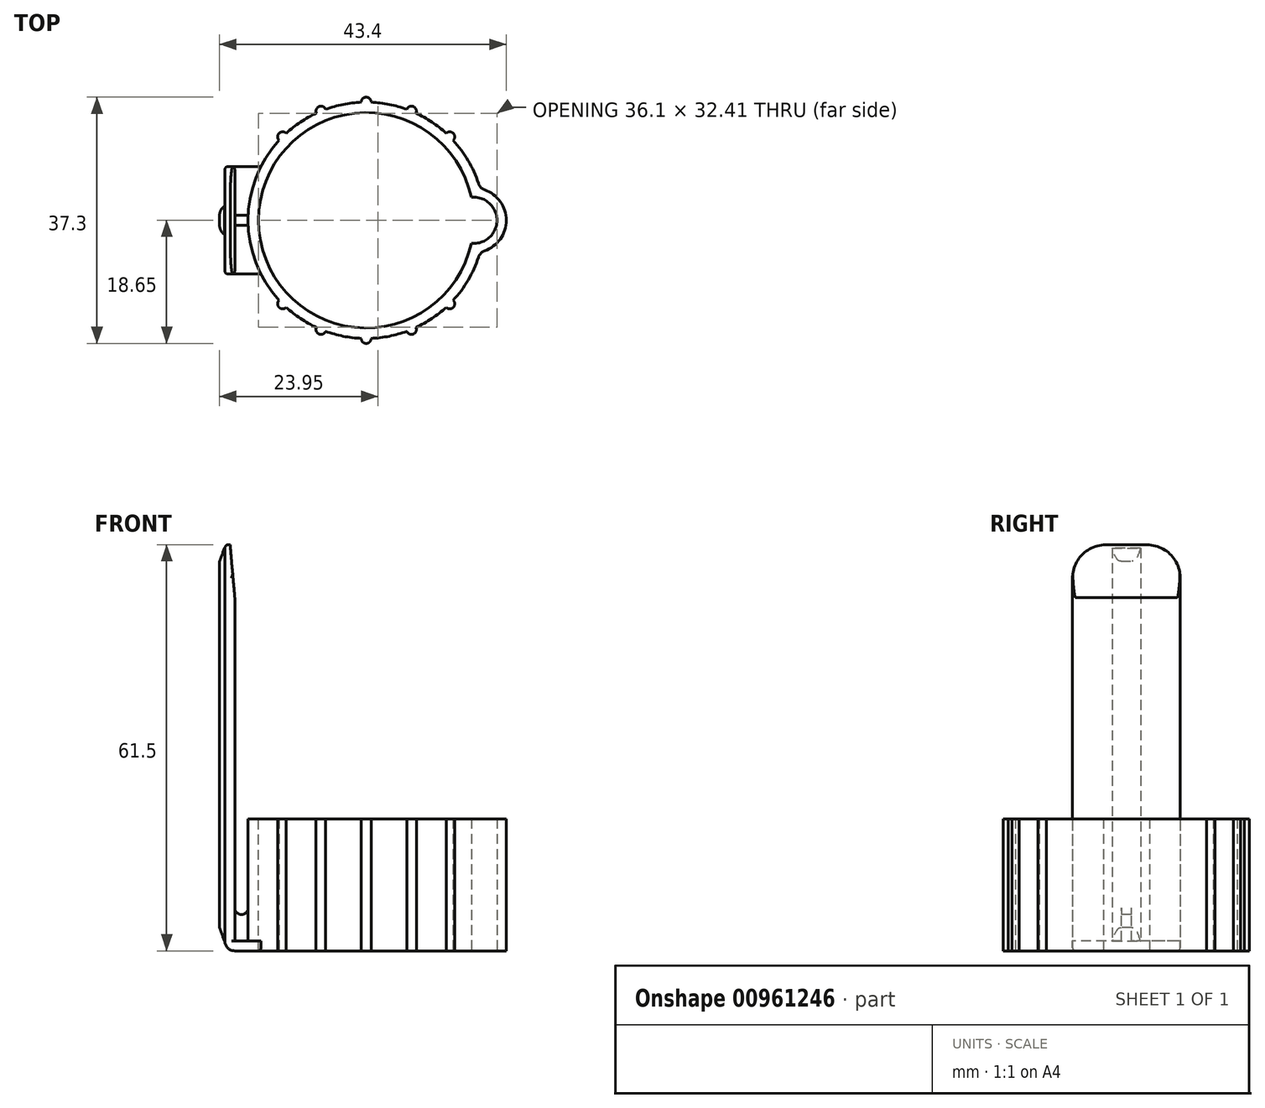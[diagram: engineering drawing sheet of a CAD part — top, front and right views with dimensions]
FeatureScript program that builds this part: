
annotation { "Feature Type Name" : "Feature", "Feature Type Description" : "" }
export const myFeature = defineFeature(function(context is Context, id is Id, definition is map)
    precondition{}
    {
        {
            var Q0;
            Q0=qCreatedBy(makeId("Top.planeOp"),FACE);
            var sketch = newSketch(context, id + "F0", { "sketchPlane" : qUnion([Q0])});
            skCircle(sketch, "E0", {"center": v(0, 0) * mm, "radius": 17.9 * mm});
            skCircle(sketch, "E1", {"center": v(0, 0) * mm, "radius": 16.3 * mm});
            skSolve(sketch);
        }
        {
            var Q0;
            Q0=makeQuery(id+"F0.imprint","IMPRINT",FACE,{"disambiguationData":[TD([[makeQuery(id+"F0.imprint","IMPRINT",EDGE,{"derivedFrom":sQuery(id+"F0.wireOp",EDGE,"E0")}),1.0]])]});
            extrude(context, id + "F1", {"entities" : qUnion([Q0]), "oppositeDirection" : true, "depth" : 20 * mm, "offsetDistance" : 25 * mm});
        }
        {
            var Q0;
            Q0=makeQuery(id+"F1.opExtrude","CAP_FACE",FACE,{"disambiguationData":[OSD([sQuery(id+"F0.wireOp",EDGE,"E0"),sQuery(id+"F0.wireOp",EDGE,"sRQzcW8V-2rlP-Dt0l-GWwx-olrQuQmdxicd")])],"isStart":false});
            var sketch = newSketch(context, id + "F2", { "sketchPlane" : qUnion([Q0])});
            skCircle(sketch, "E2.0", {"center": v(0, 0) * mm, "radius": 17.9 * mm});
            skCircle(sketch, "E3", {"center": v(0, 17.9) * mm, "radius": 0.75 * mm});
            skCircle(sketch, "E4.1.0", {"center": v(-6.85, 16.54) * mm, "radius": 0.75 * mm});
            skCircle(sketch, "E4.2.0", {"center": v(-12.66, 12.66) * mm, "radius": 0.75 * mm});
            skCircle(sketch, "E4.6.0", {"center": v(-12.66, -12.66) * mm, "radius": 0.75 * mm});
            skCircle(sketch, "E4.7.0", {"center": v(-6.85, -16.54) * mm, "radius": 0.75 * mm});
            skCircle(sketch, "E5.1.8.0", {"center": v(0, -17.9) * mm, "radius": 0.75 * mm});
            skCircle(sketch, "E5.1.9.0", {"center": v(6.85, -16.54) * mm, "radius": 0.75 * mm});
            skCircle(sketch, "E5.1.10.0", {"center": v(12.66, -12.66) * mm, "radius": 0.75 * mm});
            skCircle(sketch, "E5.1.11.0", {"center": v(16.54, -6.85) * mm, "radius": 0.75 * mm});
            skCircle(sketch, "E5.1.13.0", {"center": v(16.54, 6.85) * mm, "radius": 0.75 * mm});
            skCircle(sketch, "E5.1.14.0", {"center": v(12.66, 12.66) * mm, "radius": 0.75 * mm});
            skCircle(sketch, "E5.1.15.0", {"center": v(6.85, 16.54) * mm, "radius": 0.75 * mm});
            skLineSegment(sketch, "E6", {"start": v(0, 0) * mm, "end": v(19.2, 0) * mm});
            skLineSegment(sketch, "E7", {"start": v(0, 0) * mm, "end": v(-19.9, 0) * mm});
            skCircle(sketch, "E8.1.0", {"center": v(-16.54, 6.85) * mm, "radius": 0.75 * mm});
            skCircle(sketch, "E8.2.0", {"center": v(-17.9, 0) * mm, "radius": 0.75 * mm});
            skCircle(sketch, "E8.3.0", {"center": v(-16.54, -6.85) * mm, "radius": 0.75 * mm});
            skLineSegment(sketch, "E8.anchor1", {"start": v(0, 0) * mm, "end": v(-12.66, 12.66) * mm, "construction": true});
            skLineSegment(sketch, "E8.anchor2", {"start": v(0, 0) * mm, "end": v(-12.66, -12.66) * mm, "construction": true});
            skLineSegment(sketch, "E9", {"start": v(-21.4, 8.15) * mm, "end": v(-21.4, -8.15) * mm});
            skCircle(sketch, "E10", {"center": v(16.3, 0) * mm, "radius": 3.5 * mm});
            skCircle(sketch, "E11.0", {"center": v(16.3, 0) * mm, "radius": 4.9 * mm});
            skLineSegment(sketch, "E12", {"start": v(-21.4, 8.15) * mm, "end": v(-15.94, 8.15) * mm});
            skLineSegment(sketch, "E13.MirrorCS", {"start": v(-21.4, -8.15) * mm, "end": v(-15.94, -8.15) * mm});
            skSolve(sketch);
        }
        {
            var Q0;
            {var subQ0=sQuery(id+"F2.wireOp",EDGE,"E5.1.10.0");var subQ1=sQuery(id+"F2.wireOp",EDGE,"E2.0");var subQ2=makeQuery(id+"F2.imprint","INTERSECT",VERTEX,{"disambiguationData":[OD(0.0)],"derivedFrom":[subQ1,subQ0]});Q0=makeQuery(id+"F2.imprint","IMPRINT",FACE,{"disambiguationData":[TD([[makeQuery(id+"F2.imprint","IMPRINT",EDGE,{"disambiguationData":[TD([[subQ2,-1.0]])],"derivedFrom":subQ1}),1.0]])]});}
            var Q1;
            {var subQ0=sQuery(id+"F2.wireOp",EDGE,"E5.1.9.0");var subQ1=sQuery(id+"F2.wireOp",EDGE,"E2.0");var subQ2=makeQuery(id+"F2.imprint","INTERSECT",VERTEX,{"disambiguationData":[OD(0.0)],"derivedFrom":[subQ1,subQ0]});Q1=makeQuery(id+"F2.imprint","IMPRINT",FACE,{"disambiguationData":[TD([[makeQuery(id+"F2.imprint","IMPRINT",EDGE,{"disambiguationData":[TD([[subQ2,-1.0]])],"derivedFrom":subQ1}),1.0]])]});}
            var Q2;
            {var subQ0=sQuery(id+"F2.wireOp",EDGE,"E5.1.8.0");var subQ1=sQuery(id+"F2.wireOp",EDGE,"E2.0");var subQ2=makeQuery(id+"F2.imprint","INTERSECT",VERTEX,{"disambiguationData":[OD(0.0)],"derivedFrom":[subQ1,subQ0]});Q2=makeQuery(id+"F2.imprint","IMPRINT",FACE,{"disambiguationData":[TD([[makeQuery(id+"F2.imprint","IMPRINT",EDGE,{"disambiguationData":[TD([[subQ2,-1.0]])],"derivedFrom":subQ1}),1.0]])]});}
            var Q3;
            {var subQ0=sQuery(id+"F2.wireOp",EDGE,"E4.7.0");var subQ1=sQuery(id+"F2.wireOp",EDGE,"E2.0");var subQ2=makeQuery(id+"F2.imprint","INTERSECT",VERTEX,{"disambiguationData":[OD(0.0)],"derivedFrom":[subQ1,subQ0]});Q3=makeQuery(id+"F2.imprint","IMPRINT",FACE,{"disambiguationData":[TD([[makeQuery(id+"F2.imprint","IMPRINT",EDGE,{"disambiguationData":[TD([[subQ2,-1.0]])],"derivedFrom":subQ1}),1.0]])]});}
            var Q4;
            {var subQ0=sQuery(id+"F2.wireOp",EDGE,"E4.6.0");var subQ1=sQuery(id+"F2.wireOp",EDGE,"E2.0");var subQ2=makeQuery(id+"F2.imprint","INTERSECT",VERTEX,{"disambiguationData":[OD(0.0)],"derivedFrom":[subQ1,subQ0]});Q4=makeQuery(id+"F2.imprint","IMPRINT",FACE,{"disambiguationData":[TD([[makeQuery(id+"F2.imprint","IMPRINT",EDGE,{"disambiguationData":[TD([[subQ2,-1.0]])],"derivedFrom":subQ1}),1.0]])]});}
            var Q5;
            {var subQ0=sQuery(id+"F2.wireOp",EDGE,"E4.5.0");var subQ1=sQuery(id+"F2.wireOp",EDGE,"E2.0");var subQ2=makeQuery(id+"F2.imprint","INTERSECT",VERTEX,{"disambiguationData":[OD(0.0)],"derivedFrom":[subQ1,subQ0]});Q5=makeQuery(id+"F2.imprint","IMPRINT",FACE,{"disambiguationData":[TD([[makeQuery(id+"F2.imprint","IMPRINT",EDGE,{"disambiguationData":[TD([[subQ2,-1.0]])],"derivedFrom":subQ1}),1.0]])]});}
            var Q6;
            {var subQ0=sQuery(id+"F2.wireOp",EDGE,"E4.4.0");var subQ1=sQuery(id+"F2.wireOp",EDGE,"E2.0");var subQ2=makeQuery(id+"F2.imprint","INTERSECT",VERTEX,{"disambiguationData":[OD(0.0)],"derivedFrom":[subQ1,subQ0]});Q6=makeQuery(id+"F2.imprint","IMPRINT",FACE,{"disambiguationData":[TD([[makeQuery(id+"F2.imprint","IMPRINT",EDGE,{"disambiguationData":[TD([[subQ2,-1.0]])],"derivedFrom":subQ1}),1.0]])]});}
            var Q7;
            {var subQ0=sQuery(id+"F2.wireOp",EDGE,"E4.3.0");var subQ1=sQuery(id+"F2.wireOp",EDGE,"E2.0");var subQ2=makeQuery(id+"F2.imprint","INTERSECT",VERTEX,{"disambiguationData":[OD(0.0)],"derivedFrom":[subQ1,subQ0]});Q7=makeQuery(id+"F2.imprint","IMPRINT",FACE,{"disambiguationData":[TD([[makeQuery(id+"F2.imprint","IMPRINT",EDGE,{"disambiguationData":[TD([[subQ2,-1.0]])],"derivedFrom":subQ1}),1.0]])]});}
            var Q8;
            {var subQ0=sQuery(id+"F2.wireOp",EDGE,"E4.2.0");var subQ1=sQuery(id+"F2.wireOp",EDGE,"E2.0");var subQ2=makeQuery(id+"F2.imprint","INTERSECT",VERTEX,{"disambiguationData":[OD(0.0)],"derivedFrom":[subQ1,subQ0]});Q8=makeQuery(id+"F2.imprint","IMPRINT",FACE,{"disambiguationData":[TD([[makeQuery(id+"F2.imprint","IMPRINT",EDGE,{"disambiguationData":[TD([[subQ2,-1.0]])],"derivedFrom":subQ1}),1.0]])]});}
            var Q9;
            {var subQ0=sQuery(id+"F2.wireOp",EDGE,"E4.1.0");var subQ1=sQuery(id+"F2.wireOp",EDGE,"E2.0");var subQ2=makeQuery(id+"F2.imprint","INTERSECT",VERTEX,{"disambiguationData":[OD(0.0)],"derivedFrom":[subQ1,subQ0]});Q9=makeQuery(id+"F2.imprint","IMPRINT",FACE,{"disambiguationData":[TD([[makeQuery(id+"F2.imprint","IMPRINT",EDGE,{"disambiguationData":[TD([[subQ2,-1.0]])],"derivedFrom":subQ1}),1.0]])]});}
            var Q10;
            {var subQ0=sQuery(id+"F2.wireOp",EDGE,"E3");var subQ1=sQuery(id+"F2.wireOp",EDGE,"E2.0");var subQ2=makeQuery(id+"F2.imprint","INTERSECT",VERTEX,{"disambiguationData":[OD(0.0)],"derivedFrom":[subQ1,subQ0]});Q10=makeQuery(id+"F2.imprint","IMPRINT",FACE,{"disambiguationData":[TD([[makeQuery(id+"F2.imprint","IMPRINT",EDGE,{"disambiguationData":[TD([[subQ2,-1.0]])],"derivedFrom":subQ1}),1.0]])]});}
            var Q11;
            {var subQ0=sQuery(id+"F2.wireOp",EDGE,"E5.1.15.0");var subQ1=sQuery(id+"F2.wireOp",EDGE,"E2.0");var subQ2=makeQuery(id+"F2.imprint","INTERSECT",VERTEX,{"disambiguationData":[OD(0.0)],"derivedFrom":[subQ1,subQ0]});Q11=makeQuery(id+"F2.imprint","IMPRINT",FACE,{"disambiguationData":[TD([[makeQuery(id+"F2.imprint","IMPRINT",EDGE,{"disambiguationData":[TD([[subQ2,-1.0]])],"derivedFrom":subQ1}),1.0]])]});}
            var Q12;
            {var subQ0=sQuery(id+"F2.wireOp",EDGE,"E5.1.14.0");var subQ1=sQuery(id+"F2.wireOp",EDGE,"E2.0");var subQ2=makeQuery(id+"F2.imprint","INTERSECT",VERTEX,{"disambiguationData":[OD(0.0)],"derivedFrom":[subQ1,subQ0]});Q12=makeQuery(id+"F2.imprint","IMPRINT",FACE,{"disambiguationData":[TD([[makeQuery(id+"F2.imprint","IMPRINT",EDGE,{"disambiguationData":[TD([[subQ2,-1.0]])],"derivedFrom":subQ1}),1.0]])]});}
            var Q13;
            {var subQ0=sQuery(id+"F2.wireOp",EDGE,"E5.1.12.0");var subQ1=sQuery(id+"F2.wireOp",EDGE,"E2.0");var subQ2=makeQuery(id+"F2.imprint","INTERSECT",VERTEX,{"disambiguationData":[OD(0.0)],"derivedFrom":[subQ1,subQ0]});Q13=makeQuery(id+"F2.imprint","IMPRINT",FACE,{"disambiguationData":[TD([[makeQuery(id+"F2.imprint","IMPRINT",EDGE,{"disambiguationData":[TD([[subQ2,1.0]])],"derivedFrom":subQ1}),1.0]])]});}
            var Q14;
            {var subQ0=sQuery(id+"F2.wireOp",EDGE,"386c1725-cd85-426e-880f-386daac7d9d5.0");var subQ1=sQuery(id+"F2.wireOp",EDGE,"E2.0");var subQ2=makeQuery(id+"F2.imprint","INTERSECT",VERTEX,{"disambiguationData":[OD(0.0)],"derivedFrom":[subQ1,subQ0]});Q14=makeQuery(id+"F2.imprint","IMPRINT",FACE,{"disambiguationData":[TD([[makeQuery(id+"F2.imprint","IMPRINT",EDGE,{"disambiguationData":[TD([[subQ2,1.0]])],"derivedFrom":subQ1}),1.0]])]});}
            var Q15;
            {var subQ0=sQuery(id+"F2.wireOp",EDGE,"E4.6.0");var subQ1=sQuery(id+"F2.wireOp",EDGE,"E2.0");var subQ2=makeQuery(id+"F2.imprint","INTERSECT",VERTEX,{"disambiguationData":[OD(0.0)],"derivedFrom":[subQ1,subQ0]});Q15=makeQuery(id+"F2.imprint","IMPRINT",FACE,{"disambiguationData":[TD([[makeQuery(id+"F2.imprint","IMPRINT",EDGE,{"disambiguationData":[TD([[subQ2,-1.0]])],"derivedFrom":subQ1}),1.0]])]});}
            var Q16;
            {var subQ0=sQuery(id+"F2.wireOp",EDGE,"E11.0");var subQ1=sQuery(id+"F2.wireOp",EDGE,"E2.0");var subQ2=makeQuery(id+"F2.imprint","INTERSECT",VERTEX,{"disambiguationData":[OD(0.0)],"derivedFrom":[subQ1,subQ0]});Q16=makeQuery(id+"F2.imprint","IMPRINT",FACE,{"disambiguationData":[TD([[makeQuery(id+"F2.imprint","IMPRINT",EDGE,{"disambiguationData":[TD([[subQ2,1.0]])],"derivedFrom":subQ1}),1.0]])]});}
            var Q17;
            Q17=makeQuery(id+"F1.opExtrude","CAP_FACE",FACE,{"disambiguationData":[OSD([sQuery(id+"F0.wireOp",EDGE,"E0"),sQuery(id+"F0.wireOp",EDGE,"E1")])],"isStart":true});
            extrude(context, id + "F3", {"entities" : qUnion([Q0, Q1, Q2, Q3, Q4, Q5, Q6, Q7, Q8, Q9, Q10, Q11, Q12, Q13, Q14, Q15, Q16]), "operationType" : NewBodyOperationType.ADD, "endBound" : BoundingType.UP_TO_SURFACE, "oppositeDirection" : true, "depth" : 25 * mm, "endBoundEntityFace" : qUnion([Q17]), "offsetDistance" : 25 * mm});
        }
        {
            var Q0;
            {var subQ0=sQuery(id+"F2.wireOp",EDGE,"E2.0");Q0=makeQuery(id+"F3.boolean.opBoolean","MERGE",FACE,{"derivedFrom":[makeQuery(id+"FnFO8i2DjUKFFR7_0.opExtrude","CAP_FACE",FACE,{"disambiguationData":[OSD([sQuery(id+"F0.wireOp",EDGE,"E0"),sQuery(id+"F0.wireOp",EDGE,"E1")])],"isStart":false}),makeQuery(id+"F3.opExtrude","CAP_FACE",FACE,{"disambiguationData":[OSD([subQ0,sQuery(id+"F2.wireOp",EDGE,"E5.1.11.0")])],"isStart":false}),makeQuery(id+"F3.opExtrude","CAP_FACE",FACE,{"disambiguationData":[OSD([subQ0,sQuery(id+"F2.wireOp",EDGE,"E5.1.10.0")])],"isStart":false}),makeQuery(id+"F3.opExtrude","CAP_FACE",FACE,{"disambiguationData":[OSD([subQ0,sQuery(id+"F2.wireOp",EDGE,"E5.1.9.0")])],"isStart":false}),makeQuery(id+"F3.opExtrude","CAP_FACE",FACE,{"disambiguationData":[OSD([subQ0,sQuery(id+"F2.wireOp",EDGE,"E5.1.8.0")])],"isStart":false}),makeQuery(id+"F3.opExtrude","CAP_FACE",FACE,{"disambiguationData":[OSD([subQ0,sQuery(id+"F2.wireOp",EDGE,"E4.7.0")])],"isStart":false}),makeQuery(id+"F3.opExtrude","CAP_FACE",FACE,{"disambiguationData":[OSD([subQ0,sQuery(id+"F2.wireOp",EDGE,"E4.6.0")])],"isStart":false}),makeQuery(id+"F3.opExtrude","CAP_FACE",FACE,{"disambiguationData":[OSD([subQ0,sQuery(id+"F2.wireOp",EDGE,"E4.5.0")])],"isStart":false}),makeQuery(id+"F3.opExtrude","CAP_FACE",FACE,{"disambiguationData":[OSD([subQ0,sQuery(id+"F2.wireOp",EDGE,"E4.4.0")])],"isStart":false}),makeQuery(id+"F3.opExtrude","CAP_FACE",FACE,{"disambiguationData":[OSD([subQ0,sQuery(id+"F2.wireOp",EDGE,"E4.3.0")])],"isStart":false}),makeQuery(id+"F3.opExtrude","CAP_FACE",FACE,{"disambiguationData":[OSD([subQ0,sQuery(id+"F2.wireOp",EDGE,"E4.2.0")])],"isStart":false}),makeQuery(id+"F3.opExtrude","CAP_FACE",FACE,{"disambiguationData":[OSD([subQ0,sQuery(id+"F2.wireOp",EDGE,"E4.1.0")])],"isStart":false}),makeQuery(id+"F3.opExtrude","CAP_FACE",FACE,{"disambiguationData":[OSD([subQ0,sQuery(id+"F2.wireOp",EDGE,"E3")])],"isStart":false}),makeQuery(id+"F3.opExtrude","CAP_FACE",FACE,{"disambiguationData":[OSD([subQ0,sQuery(id+"F2.wireOp",EDGE,"E5.1.15.0")])],"isStart":false}),makeQuery(id+"F3.opExtrude","CAP_FACE",FACE,{"disambiguationData":[OSD([subQ0,sQuery(id+"F2.wireOp",EDGE,"E5.1.14.0")])],"isStart":false}),makeQuery(id+"F3.opExtrude","CAP_FACE",FACE,{"disambiguationData":[OSD([subQ0,sQuery(id+"F2.wireOp",EDGE,"E5.1.13.0")])],"isStart":false}),makeQuery(id+"F3.opExtrude","CAP_FACE",FACE,{"disambiguationData":[OSD([subQ0,sQuery(id+"F2.wireOp",EDGE,"E5.1.12.0")])],"isStart":false})]});}
            var sketch = newSketch(context, id + "F4", { "sketchPlane" : qUnion([Q0])});
            skCircle(sketch, "E14", {"center": v(0, 0) * mm, "radius": 16.8 * mm});
            skArc(sketch, "E15.0", {"start": v(12.11, 13.18) * mm, "mid": v(9.94, 14.88) * mm, "end": v(7.54, 16.23) * mm});
            skSolve(sketch);
        }
        {
            var Q0;
            {var subQ0=sQuery(id+"F2.wireOp",EDGE,"E8.1.0");var subQ1=sQuery(id+"F2.wireOp",EDGE,"E2.0");var subQ2=makeQuery(id+"F2.imprint","INTERSECT",VERTEX,{"disambiguationData":[OD(0.0)],"derivedFrom":[subQ1,subQ0]});Q0=makeQuery(id+"F2.imprint","IMPRINT",FACE,{"disambiguationData":[TD([[makeQuery(id+"F2.imprint","IMPRINT",EDGE,{"disambiguationData":[TD([[subQ2,-1.0]])],"derivedFrom":subQ1}),1.0]])]});}
            var Q1;
            {var subQ0=sQuery(id+"F2.wireOp",EDGE,"E7");var subQ1=sQuery(id+"F2.wireOp",EDGE,"E2.0");var subQ2=makeQuery(id+"F2.imprint","INTERSECT",VERTEX,{"derivedFrom":[subQ1,subQ0]});Q1=makeQuery(id+"F2.imprint","IMPRINT",FACE,{"disambiguationData":[TD([[makeQuery(id+"F2.imprint","IMPRINT",EDGE,{"disambiguationData":[TD([[subQ2,-1.0]])],"derivedFrom":subQ1}),1.0]])]});}
            var Q2;
            {var subQ0=sQuery(id+"F2.wireOp",EDGE,"E8.2.0");var subQ1=sQuery(id+"F2.wireOp",EDGE,"E2.0");var subQ2=makeQuery(id+"F2.imprint","INTERSECT",VERTEX,{"disambiguationData":[OD(0.0)],"derivedFrom":[subQ1,subQ0]});Q2=makeQuery(id+"F2.imprint","IMPRINT",FACE,{"disambiguationData":[TD([[makeQuery(id+"F2.imprint","IMPRINT",EDGE,{"disambiguationData":[TD([[subQ2,-1.0]])],"derivedFrom":subQ1}),1.0]])]});}
            var Q3;
            {var subQ0=sQuery(id+"F2.wireOp",EDGE,"E8.3.0");var subQ1=sQuery(id+"F2.wireOp",EDGE,"E2.0");var subQ2=makeQuery(id+"F2.imprint","INTERSECT",VERTEX,{"disambiguationData":[OD(0.0)],"derivedFrom":[subQ1,subQ0]});Q3=makeQuery(id+"F2.imprint","IMPRINT",FACE,{"disambiguationData":[TD([[makeQuery(id+"F2.imprint","IMPRINT",EDGE,{"disambiguationData":[TD([[subQ2,-1.0]])],"derivedFrom":subQ1}),1.0]])]});}
            var Q4;
            Q4=makeQuery(id+"F2.imprint","IMPRINT",FACE,{"disambiguationData":[TD([[makeQuery(id+"F2.imprint","IMPRINT",EDGE,{"derivedFrom":sQuery(id+"F2.wireOp",EDGE,"E9")}),1.0]])]});
            extrude(context, id + "F5", {"entities" : qUnion([Q0, Q1, Q2, Q3, Q4]), "operationType" : NewBodyOperationType.ADD, "oppositeDirection" : true, "depth" : 1.5 * mm, "offsetDistance" : 25 * mm});
        }
        {
            var Q0;
            {var subQ0=sQuery(id+"F2.wireOp",EDGE,"E6");var subQ1=sQuery(id+"F2.wireOp",EDGE,"E2.0");var subQ2=makeQuery(id+"F2.imprint","INTERSECT",VERTEX,{"derivedFrom":[subQ1,subQ0]});Q0=makeQuery(id+"F2.imprint","IMPRINT",FACE,{"disambiguationData":[TD([[makeQuery(id+"F2.imprint","IMPRINT",EDGE,{"disambiguationData":[TD([[subQ2,1.0]])],"derivedFrom":subQ1}),-1.0]])]});}
            var Q1;
            {var subQ0=sQuery(id+"F2.wireOp",EDGE,"E6");var subQ1=sQuery(id+"F2.wireOp",EDGE,"E2.0");var subQ2=makeQuery(id+"F2.imprint","INTERSECT",VERTEX,{"derivedFrom":[subQ1,subQ0]});Q1=makeQuery(id+"F2.imprint","IMPRINT",FACE,{"disambiguationData":[TD([[makeQuery(id+"F2.imprint","IMPRINT",EDGE,{"disambiguationData":[TD([[subQ2,-1.0]])],"derivedFrom":subQ1}),-1.0]])]});}
            extrude(context, id + "F6", {"entities" : qUnion([Q0, Q1]), "operationType" : NewBodyOperationType.REMOVE, "oppositeDirection" : true, "depth" : 25 * mm, "offsetDistance" : 25 * mm});
        }
        {
            var Q0;
            {var subQ0=sQuery(id+"F2.wireOp",EDGE,"E11.0");var subQ1=sQuery(id+"F2.wireOp",EDGE,"E2.0");Q0=makeQuery(id+"F3.opExtrude","SWEPT_EDGE",EDGE,{"disambiguationData":[OSD([subQ1,subQ0]),TDD([makeQuery(id+"F2.imprint","INTERSECT",VERTEX,{"disambiguationData":[OD(1.0)],"derivedFrom":[subQ1,subQ0]})])]});}
            var Q1;
            {var subQ0=sQuery(id+"F2.wireOp",EDGE,"E11.0");var subQ1=sQuery(id+"F2.wireOp",EDGE,"E2.0");Q1=makeQuery(id+"F3.opExtrude","SWEPT_EDGE",EDGE,{"disambiguationData":[OSD([subQ1,subQ0]),TDD([makeQuery(id+"F2.imprint","INTERSECT",VERTEX,{"disambiguationData":[OD(0.0)],"derivedFrom":[subQ1,subQ0]})])]});}
            var Q2;
            {var subQ0=sQuery(id+"F2.wireOp",EDGE,"E10");var subQ1=sQuery(id+"F0.wireOp",EDGE,"E1");Q2=makeQuery(id+"F6.boolean.opBoolean","COPY",EDGE,{"derivedFrom":makeQuery(id+"F6.opExtrude","SWEPT_EDGE",EDGE,{"disambiguationData":[OSD([subQ1,subQ0]),TDD([makeQuery(id+"F2.imprint","INTERSECT",VERTEX,{"disambiguationData":[OD(1.0)],"derivedFrom":[makeQuery(id+"F1.opExtrude","CAP_EDGE",EDGE,{"disambiguationData":[OSD([subQ1])],"isStart":false}),subQ0]})])]})});}
            var Q3;
            {var subQ0=sQuery(id+"F2.wireOp",EDGE,"E10");var subQ1=sQuery(id+"F0.wireOp",EDGE,"E1");Q3=makeQuery(id+"F6.boolean.opBoolean","COPY",EDGE,{"derivedFrom":makeQuery(id+"F6.opExtrude","SWEPT_EDGE",EDGE,{"disambiguationData":[OSD([subQ1,subQ0]),TDD([makeQuery(id+"F2.imprint","INTERSECT",VERTEX,{"disambiguationData":[OD(0.0)],"derivedFrom":[makeQuery(id+"F1.opExtrude","CAP_EDGE",EDGE,{"disambiguationData":[OSD([subQ1])],"isStart":false}),subQ0]})])]})});}
            fillet(context, id + "F7", {"entities" : qUnion([Q0, Q1, Q2, Q3]), "radius" : 1.5 * mm, "tangentPropagation" : true, "defaultsChanged" : false, "vertexSettings" : [], "allowEdgeOverflow" : false});
        }
        {
            var Q0;
            Q0=qCreatedBy(makeId("Front.planeOp"),FACE);
            var sketch = newSketch(context, id + "F8", { "sketchPlane" : qUnion([Q0])});
            skLineSegment(sketch, "E16.bottom", {"start": v(-41.01, 64.42) * mm, "end": v(41.01, 64.42) * mm});
            skLineSegment(sketch, "E16.top", {"start": v(-41.01, -64.42) * mm, "end": v(41.01, -64.42) * mm});
            skLineSegment(sketch, "E16.left", {"start": v(-41.01, 64.42) * mm, "end": v(-41.01, -64.42) * mm});
            skLineSegment(sketch, "E16.right", {"start": v(41.01, 64.42) * mm, "end": v(41.01, -64.42) * mm});
            skPoint(sketch, "E16.middle", {"position": v(0, 0) * mm});
            skSolve(sketch);
        }
        {
            var Q0;
            Q0=makeQuery(id+"F5.opExtrude","CAP_FACE",FACE,{"disambiguationData":[OSD([sQuery(id+"F2.wireOp",EDGE,"E2.0"),sQuery(id+"F2.wireOp",EDGE,"E9"),sQuery(id+"F2.wireOp",EDGE,"E12"),sQuery(id+"F2.wireOp",EDGE,"E13.MirrorCS")])],"isStart":false});
            var sketch = newSketch(context, id + "F9", { "sketchPlane" : qUnion([Q0])});
            skLineSegment(sketch, "E17.bottom", {"start": v(-21.4, 8.15) * mm, "end": v(-19.9, 8.15) * mm});
            skLineSegment(sketch, "E17.top", {"start": v(-21.4, -8.15) * mm, "end": v(-19.9, -8.15) * mm});
            skLineSegment(sketch, "E17.left", {"start": v(-21.4, 8.15) * mm, "end": v(-21.4, -8.15) * mm});
            skLineSegment(sketch, "E17.right", {"start": v(-19.9, 8.15) * mm, "end": v(-19.9, -8.15) * mm});
            skSolve(sketch);
        }
        {
            var Q0;
            Q0=makeQuery(id+"F9.imprint","IMPRINT",FACE,{"disambiguationData":[TD([[makeQuery(id+"F9.imprint","IMPRINT",EDGE,{"derivedFrom":sQuery(id+"F9.wireOp",EDGE,"E17.bottom")}),-1.0]])]});
            extrude(context, id + "F10", {"entities" : qUnion([Q0]), "operationType" : NewBodyOperationType.ADD, "depth" : 60 * mm, "offsetDistance" : 25 * mm});
        }
        {
            var Q0;
            Q0=makeQuery(id+"F10.opExtrude","CAP_EDGE",EDGE,{"disambiguationData":[OSD([sQuery(id+"F9.wireOp",EDGE,"E17.bottom")])],"isStart":false});
            var Q1;
            Q1=makeQuery(id+"F10.opExtrude","CAP_EDGE",EDGE,{"disambiguationData":[OSD([sQuery(id+"F9.wireOp",EDGE,"E17.top")])],"isStart":false});
            fillet(context, id + "F11", {"entities" : qUnion([Q0, Q1]), "radius" : 5 * mm, "tangentPropagation" : true, "allowEdgeOverflow" : false});
        }
        {
            var Q0;
            Q0=makeQuery(id+"F5.opExtrude","CAP_EDGE",EDGE,{"disambiguationData":[OSD([sQuery(id+"F2.wireOp",EDGE,"E9")])],"isStart":true});
            var Q1;
            Q1=makeQuery(id+"F10.opExtrude","CAP_EDGE",EDGE,{"disambiguationData":[OSD([sQuery(id+"F9.wireOp",EDGE,"E17.right")])],"isStart":true});
            var Q2;
            {var subQ0=sQuery(id+"F2.wireOp",EDGE,"E2.0");var subQ1=sQuery(id+"F2.wireOp",EDGE,"E8.1.0");var subQ3=makeQuery(id+"F2.imprint","INTERSECT",VERTEX,{"disambiguationData":[OD(0.0)],"derivedFrom":[subQ0,subQ1]});var subQ4=sQuery(id+"F2.wireOp",EDGE,"E8.2.0");var subQ5=makeQuery(id+"F2.imprint","INTERSECT",VERTEX,{"disambiguationData":[OD(1.0)],"derivedFrom":[subQ0,subQ4]});var subQ6=makeQuery(id+"F2.imprint","INTERSECT",VERTEX,{"derivedFrom":[subQ0,sQuery(id+"F2.wireOp",EDGE,"E7")]});var subQ7=makeQuery(id+"F2.imprint","INTERSECT",VERTEX,{"disambiguationData":[OD(0.0)],"derivedFrom":[subQ0,subQ4]});var subQ8=sQuery(id+"F2.wireOp",EDGE,"E8.3.0");var subQ9=makeQuery(id+"F2.imprint","INTERSECT",VERTEX,{"disambiguationData":[OD(1.0)],"derivedFrom":[subQ0,subQ8]});var subQ10=makeQuery(id+"F2.imprint","INTERSECT",VERTEX,{"disambiguationData":[OD(0.0)],"derivedFrom":[subQ0,subQ8]});Q2=makeQuery(id+"F5.opExtrude","CAP_EDGE",EDGE,{"disambiguationData":[OSD([subQ0]),TDD([makeQuery(id+"F2.imprint","IMPRINT",EDGE,{"disambiguationData":[TD([[makeQuery(id+"F2.imprint","INTERSECT",VERTEX,{"derivedFrom":[subQ0,sQuery(id+"F2.wireOp",EDGE,"E13.MirrorCS")]}),-1.0]])],"derivedFrom":subQ0}),makeQuery(id+"F2.imprint","IMPRINT",EDGE,{"disambiguationData":[TD([[subQ10,-1.0]])],"derivedFrom":subQ0}),makeQuery(id+"F2.imprint","IMPRINT",EDGE,{"disambiguationData":[TD([[subQ9,-1.0]])],"derivedFrom":subQ0}),makeQuery(id+"F2.imprint","IMPRINT",EDGE,{"disambiguationData":[TD([[subQ7,-1.0]])],"derivedFrom":subQ0}),makeQuery(id+"F2.imprint","IMPRINT",EDGE,{"disambiguationData":[TD([[subQ6,-1.0]])],"derivedFrom":subQ0}),makeQuery(id+"F2.imprint","IMPRINT",EDGE,{"disambiguationData":[TD([[subQ5,-1.0]])],"derivedFrom":subQ0}),makeQuery(id+"F2.imprint","IMPRINT",EDGE,{"disambiguationData":[TD([[subQ3,-1.0]])],"derivedFrom":subQ0}),makeQuery(id+"F2.imprint","IMPRINT",EDGE,{"disambiguationData":[TD([[makeQuery(id+"F2.imprint","INTERSECT",VERTEX,{"derivedFrom":[subQ0,sQuery(id+"F2.wireOp",EDGE,"E12")]}),1.0]])],"derivedFrom":subQ0})])],"isStart":false});}
            var Q3;
            Q3=makeQuery(id+"F5.opExtrude","SWEPT_EDGE",EDGE,{"disambiguationData":[OSD([sQuery(id+"F2.wireOp",EDGE,"E2.0"),sQuery(id+"F2.wireOp",EDGE,"E12")])]});
            var Q4;
            Q4=makeQuery(id+"F5.opExtrude","SWEPT_EDGE",EDGE,{"disambiguationData":[OSD([sQuery(id+"F2.wireOp",EDGE,"E2.0"),sQuery(id+"F2.wireOp",EDGE,"E13.MirrorCS")])]});
            fillet(context, id + "F12", {"entities" : qUnion([Q0, Q1, Q2, Q3, Q4]), "radius" : 1.5 * mm, "tangentPropagation" : true, "allowEdgeOverflow" : false});
        }
        {
            var Q0;
            Q0=makeQuery(id+"F10.opExtrude","CAP_EDGE",EDGE,{"disambiguationData":[OSD([sQuery(id+"F9.wireOp",EDGE,"E17.right")])],"isStart":false});
            chamfer(context, id + "F13", {"entities" : qUnion([Q0]), "chamferType" : ChamferType.OFFSET_ANGLE, "width" : 8 * mm, "oppositeDirection" : false, "angle" : 5 * degree});
        }
        {
            var Q0;
            Q0=makeQuery(id+"F12.opFillet","SPLIT",FACE,{"disambiguationData":[OD(0.0)],"derivedFrom":makeQuery(id+"F5.opExtrude","CAP_FACE",FACE,{"disambiguationData":[OSD([sQuery(id+"F2.wireOp",EDGE,"E2.0"),sQuery(id+"F2.wireOp",EDGE,"E9"),sQuery(id+"F2.wireOp",EDGE,"E12"),sQuery(id+"F2.wireOp",EDGE,"E13.MirrorCS")])],"isStart":false})});
            var sketch = newSketch(context, id + "F14", { "sketchPlane" : qUnion([Q0])});
            skLineSegment(sketch, "E18", {"start": v(0, 0) * mm, "end": v(-24.2, 0) * mm});
            skLineSegment(sketch, "E19.bottom", {"start": v(-20.41, 0) * mm, "end": v(-17.41, 0) * mm});
            skLineSegment(sketch, "E19.top", {"start": v(-20.41, -0.75) * mm, "end": v(-17.41, -0.75) * mm});
            skLineSegment(sketch, "E19.left", {"start": v(-20.41, 0) * mm, "end": v(-20.41, -0.75) * mm});
            skLineSegment(sketch, "E19.right", {"start": v(-17.41, 0) * mm, "end": v(-17.41, -0.75) * mm});
            skLineSegment(sketch, "E20.MirrorCS", {"start": v(-20.41, 0.75) * mm, "end": v(-17.41, 0.75) * mm});
            skLineSegment(sketch, "E21.MirrorCS", {"start": v(-20.41, 0) * mm, "end": v(-20.41, 0.75) * mm});
            skLineSegment(sketch, "E22.MirrorCS", {"start": v(-17.41, 0) * mm, "end": v(-17.41, 0.75) * mm});
            skSolve(sketch);
        }
        {
            var Q0;
            Q0 = qSketchRegion(id + "F14", true);
            extrude(context, id + "F15", {"entities" : qUnion([Q0]), "operationType" : NewBodyOperationType.ADD, "depth" : 4 * mm, "offsetDistance" : 25 * mm});
        }
        {
            var Q0;
            Q0=makeQuery(id+"F15.boolean.opBoolean","INTERSECT",EDGE,{"derivedFrom":[makeQuery(id+"F10.opExtrude","SWEPT_FACE",FACE,{"disambiguationData":[OSD([sQuery(id+"F9.wireOp",EDGE,"E17.right")])]}),makeQuery(id+"F15.opExtrude","CAP_FACE",FACE,{"disambiguationData":[OSD([sQuery(id+"F14.wireOp",EDGE,"E19.top"),sQuery(id+"F14.wireOp",EDGE,"E19.left"),sQuery(id+"F14.wireOp",EDGE,"E19.right"),sQuery(id+"F14.wireOp",EDGE,"E20.MirrorCS"),sQuery(id+"F14.wireOp",EDGE,"E21.MirrorCS"),sQuery(id+"F14.wireOp",EDGE,"E22.MirrorCS")])],"isStart":false})]});
            var Q1;
            {var subQ0=sQuery(id+"F2.wireOp",EDGE,"E5.1.15.0");var subQ1=sQuery(id+"F2.wireOp",EDGE,"E2.0");var subQ2=sQuery(id+"F2.wireOp",EDGE,"E3");var subQ3=sQuery(id+"F2.wireOp",EDGE,"E4.1.0");var subQ4=sQuery(id+"F2.wireOp",EDGE,"E4.2.0");var subQ5=sQuery(id+"F2.wireOp",EDGE,"E4.6.0");var subQ6=sQuery(id+"F2.wireOp",EDGE,"E4.7.0");var subQ7=sQuery(id+"F2.wireOp",EDGE,"E11.0");var subQ8=sQuery(id+"F2.wireOp",EDGE,"E10");var subQ9=sQuery(id+"F0.wireOp",EDGE,"E1");var subQ10=sQuery(id+"F0.wireOp",EDGE,"E0");var subQ11=sQuery(id+"F2.wireOp",EDGE,"E5.1.8.0");var subQ12=sQuery(id+"F2.wireOp",EDGE,"E5.1.10.0");var subQ13=sQuery(id+"F2.wireOp",EDGE,"E5.1.9.0");var subQ14=sQuery(id+"F2.wireOp",EDGE,"E5.1.14.0");Q1=makeQuery(id+"F15.boolean.opBoolean","INTERSECT",EDGE,{"derivedFrom":[makeQuery(id+"F3.boolean.opBoolean","SPLIT",FACE,{"disambiguationData":[TD([makeQuery(id+"F1.opExtrude","CAP_FACE",FACE,{"disambiguationData":[OSD([subQ10,subQ9])],"isStart":true}),makeQuery(id+"F1.opExtrude","CAP_FACE",FACE,{"disambiguationData":[OSD([subQ10,subQ9])],"isStart":false}),makeQuery(id+"F3.opExtrude","CAP_FACE",FACE,{"disambiguationData":[OSD([subQ1,subQ8,subQ7])],"isStart":true}),makeQuery(id+"F3.opExtrude","CAP_FACE",FACE,{"disambiguationData":[OSD([subQ1,subQ8,subQ7])],"isStart":false}),makeQuery(id+"F3.opExtrude","CAP_FACE",FACE,{"disambiguationData":[OSD([subQ1,subQ12])],"isStart":true}),makeQuery(id+"F3.opExtrude","CAP_FACE",FACE,{"disambiguationData":[OSD([subQ1,subQ12])],"isStart":false}),makeQuery(id+"F3.opExtrude","CAP_FACE",FACE,{"disambiguationData":[OSD([subQ1,subQ13])],"isStart":true}),makeQuery(id+"F3.opExtrude","CAP_FACE",FACE,{"disambiguationData":[OSD([subQ1,subQ13])],"isStart":false}),makeQuery(id+"F3.opExtrude","CAP_FACE",FACE,{"disambiguationData":[OSD([subQ1,subQ11])],"isStart":true}),makeQuery(id+"F3.opExtrude","CAP_FACE",FACE,{"disambiguationData":[OSD([subQ1,subQ11])],"isStart":false}),makeQuery(id+"F3.opExtrude","CAP_FACE",FACE,{"disambiguationData":[OSD([subQ1,subQ6])],"isStart":true}),makeQuery(id+"F3.opExtrude","CAP_FACE",FACE,{"disambiguationData":[OSD([subQ1,subQ6])],"isStart":false}),makeQuery(id+"F3.opExtrude","CAP_FACE",FACE,{"disambiguationData":[OSD([subQ1,subQ5])],"isStart":true}),makeQuery(id+"F3.opExtrude","CAP_FACE",FACE,{"disambiguationData":[OSD([subQ1,subQ5])],"isStart":false}),makeQuery(id+"F3.opExtrude","CAP_FACE",FACE,{"disambiguationData":[OSD([subQ1,subQ4])],"isStart":true}),makeQuery(id+"F3.opExtrude","CAP_FACE",FACE,{"disambiguationData":[OSD([subQ1,subQ4])],"isStart":false}),makeQuery(id+"F3.opExtrude","CAP_FACE",FACE,{"disambiguationData":[OSD([subQ1,subQ3])],"isStart":true}),makeQuery(id+"F3.opExtrude","CAP_FACE",FACE,{"disambiguationData":[OSD([subQ1,subQ3])],"isStart":false}),makeQuery(id+"F3.opExtrude","CAP_FACE",FACE,{"disambiguationData":[OSD([subQ1,subQ2])],"isStart":true}),makeQuery(id+"F3.opExtrude","CAP_FACE",FACE,{"disambiguationData":[OSD([subQ1,subQ2])],"isStart":false}),makeQuery(id+"F3.opExtrude","CAP_FACE",FACE,{"disambiguationData":[OSD([subQ1,subQ0])],"isStart":true}),makeQuery(id+"F3.opExtrude","CAP_FACE",FACE,{"disambiguationData":[OSD([subQ1,subQ0])],"isStart":false}),makeQuery(id+"F3.opExtrude","CAP_FACE",FACE,{"disambiguationData":[OSD([subQ1,subQ14])],"isStart":true}),makeQuery(id+"F3.opExtrude","CAP_FACE",FACE,{"disambiguationData":[OSD([subQ1,subQ14])],"isStart":false}),makeQuery(id+"F3.opExtrude","SWEPT_FACE",FACE,{"disambiguationData":[OSD([subQ4])]}),makeQuery(id+"F3.opExtrude","SWEPT_FACE",FACE,{"disambiguationData":[OSD([subQ5])]})])],"derivedFrom":makeQuery(id+"F1.opExtrude","SWEPT_FACE",FACE,{"disambiguationData":[OSD([subQ10])]})}),makeQuery(id+"F15.opExtrude","CAP_FACE",FACE,{"disambiguationData":[OSD([sQuery(id+"F14.wireOp",EDGE,"E19.top"),sQuery(id+"F14.wireOp",EDGE,"E19.left"),sQuery(id+"F14.wireOp",EDGE,"E19.right"),sQuery(id+"F14.wireOp",EDGE,"E20.MirrorCS"),sQuery(id+"F14.wireOp",EDGE,"E21.MirrorCS"),sQuery(id+"F14.wireOp",EDGE,"E22.MirrorCS")])],"isStart":false})]});}
            fillet(context, id + "F16", {"entities" : qUnion([Q0, Q1]), "radius" : 1 * mm, "tangentPropagation" : true, "allowEdgeOverflow" : false});
        }
        {
            var Q0;
            Q0=makeQuery(id+"F10.boolean.opBoolean","MERGE",EDGE,{"derivedFrom":[makeQuery(id+"F5.opExtrude","SWEPT_EDGE",EDGE,{"disambiguationData":[OSD([sQuery(id+"F2.wireOp",EDGE,"E9"),sQuery(id+"F2.wireOp",EDGE,"E12")])]}),makeQuery(id+"F10.opExtrude","SWEPT_EDGE",EDGE,{"disambiguationData":[OSD([sQuery(id+"F9.wireOp",EDGE,"E17.top"),sQuery(id+"F9.wireOp",EDGE,"E17.left")])]})]});
            var Q1;
            Q1=makeQuery(id+"F10.opExtrude","SWEPT_EDGE",EDGE,{"disambiguationData":[OSD([sQuery(id+"F2.wireOp",EDGE,"E12"),sQuery(id+"F9.wireOp",EDGE,"E17.top"),sQuery(id+"F9.wireOp",EDGE,"E17.right")])]});
            var Q2;
            Q2=makeQuery(id+"F10.opExtrude","SWEPT_EDGE",EDGE,{"disambiguationData":[OSD([sQuery(id+"F2.wireOp",EDGE,"E13.MirrorCS"),sQuery(id+"F9.wireOp",EDGE,"E17.bottom"),sQuery(id+"F9.wireOp",EDGE,"E17.right")])]});
            fillet(context, id + "F17", {"entities" : qUnion([Q0, Q1, Q2]), "radius" : .5 * mm, "tangentPropagation" : true, "allowEdgeOverflow" : false});
        }
        {
            var Q0;
            {var subQ0=sQuery(id+"F2.wireOp",EDGE,"E2.0");Q0=makeQuery(id+"F5.boolean.opBoolean","MERGE",FACE,{"derivedFrom":[makeQuery(id+"F3.boolean.opBoolean","MERGE",FACE,{"derivedFrom":[makeQuery(id+"F1.opExtrude","CAP_FACE",FACE,{"disambiguationData":[OSD([sQuery(id+"F0.wireOp",EDGE,"E0"),sQuery(id+"F0.wireOp",EDGE,"E1")])],"isStart":false}),makeQuery(id+"F3.opExtrude","CAP_FACE",FACE,{"disambiguationData":[OSD([subQ0,sQuery(id+"F2.wireOp",EDGE,"E10"),sQuery(id+"F2.wireOp",EDGE,"E11.0")])],"isStart":true}),makeQuery(id+"F3.opExtrude","CAP_FACE",FACE,{"disambiguationData":[OSD([subQ0,sQuery(id+"F2.wireOp",EDGE,"E5.1.10.0")])],"isStart":true}),makeQuery(id+"F3.opExtrude","CAP_FACE",FACE,{"disambiguationData":[OSD([subQ0,sQuery(id+"F2.wireOp",EDGE,"E5.1.9.0")])],"isStart":true}),makeQuery(id+"F3.opExtrude","CAP_FACE",FACE,{"disambiguationData":[OSD([subQ0,sQuery(id+"F2.wireOp",EDGE,"E5.1.8.0")])],"isStart":true}),makeQuery(id+"F3.opExtrude","CAP_FACE",FACE,{"disambiguationData":[OSD([subQ0,sQuery(id+"F2.wireOp",EDGE,"E4.7.0")])],"isStart":true}),makeQuery(id+"F3.opExtrude","CAP_FACE",FACE,{"disambiguationData":[OSD([subQ0,sQuery(id+"F2.wireOp",EDGE,"E4.6.0")])],"isStart":true}),makeQuery(id+"F3.opExtrude","CAP_FACE",FACE,{"disambiguationData":[OSD([subQ0,sQuery(id+"F2.wireOp",EDGE,"E4.2.0")])],"isStart":true}),makeQuery(id+"F3.opExtrude","CAP_FACE",FACE,{"disambiguationData":[OSD([subQ0,sQuery(id+"F2.wireOp",EDGE,"E4.1.0")])],"isStart":true}),makeQuery(id+"F3.opExtrude","CAP_FACE",FACE,{"disambiguationData":[OSD([subQ0,sQuery(id+"F2.wireOp",EDGE,"E3")])],"isStart":true}),makeQuery(id+"F3.opExtrude","CAP_FACE",FACE,{"disambiguationData":[OSD([subQ0,sQuery(id+"F2.wireOp",EDGE,"E5.1.15.0")])],"isStart":true}),makeQuery(id+"F3.opExtrude","CAP_FACE",FACE,{"disambiguationData":[OSD([subQ0,sQuery(id+"F2.wireOp",EDGE,"E5.1.14.0")])],"isStart":true})]}),makeQuery(id+"F5.opExtrude","CAP_FACE",FACE,{"disambiguationData":[OSD([subQ0,sQuery(id+"F2.wireOp",EDGE,"E9"),sQuery(id+"F2.wireOp",EDGE,"E12"),sQuery(id+"F2.wireOp",EDGE,"E13.MirrorCS")])],"isStart":true})]});}
            var sketch = newSketch(context, id + "F18", { "sketchPlane" : qUnion([Q0])});
            skLineSegment(sketch, "E23.bottom", {"start": v(-22.2, 2.15) * mm, "end": v(-20.73, 2.15) * mm});
            skLineSegment(sketch, "E23.top", {"start": v(-22.2, -2.15) * mm, "end": v(-20.73, -2.15) * mm});
            skLineSegment(sketch, "E23.left", {"start": v(-22.2, 2.15) * mm, "end": v(-22.2, -2.15) * mm});
            skLineSegment(sketch, "E23.right", {"start": v(-20.73, 2.15) * mm, "end": v(-20.73, -2.15) * mm});
            skSolve(sketch);
        }
        {
            var Q0;
            Q0=makeQuery(id+"F18.imprint","IMPRINT",FACE,{"disambiguationData":[TD([[makeQuery(id+"F18.imprint","IMPRINT",EDGE,{"derivedFrom":sQuery(id+"F18.wireOp",EDGE,"E23.bottom")}),-1.0]])]});
            extrude(context, id + "F19", {"entities" : qUnion([Q0]), "operationType" : NewBodyOperationType.ADD, "oppositeDirection" : true, "depth" : 61 * mm, "offsetDistance" : 25 * mm, "hasSecondDirection" : true, "secondDirectionOppositeDirection" : true, "secondDirectionDepth" : 1.5 * mm});
        }
        {
            var Q0;
            Q0=makeQuery(id+"F19.opExtrude","CAP_EDGE",EDGE,{"disambiguationData":[OSD([sQuery(id+"F18.wireOp",EDGE,"E23.left")])],"isStart":false});
            var Q1;
            Q1=makeQuery(id+"F19.opExtrude","CAP_EDGE",EDGE,{"disambiguationData":[OSD([sQuery(id+"F18.wireOp",EDGE,"E23.left")])],"isStart":true});
            chamfer(context, id + "F20", {"entities" : qUnion([Q0, Q1]), "chamferType" : ChamferType.OFFSET_ANGLE, "width" : 2 * mm, "oppositeDirection" : false, "angle" : 20 * degree, "tangentPropagation" : true});
        }
        {
            var Q0;
            Q0=makeQuery(id+"F19.opExtrude","SWEPT_EDGE",EDGE,{"disambiguationData":[OSD([sQuery(id+"F18.wireOp",EDGE,"E23.top"),sQuery(id+"F18.wireOp",EDGE,"E23.left")])]});
            var Q1;
            Q1=makeQuery(id+"F19.opExtrude","SWEPT_EDGE",EDGE,{"disambiguationData":[OSD([sQuery(id+"F18.wireOp",EDGE,"E23.bottom"),sQuery(id+"F18.wireOp",EDGE,"E23.left")])]});
            fillet(context, id + "F21", {"entities" : qUnion([Q0, Q1]), "tangentPropagation" : true, "radius" : 1.5 * mm, "defaultsChanged" : false, "vertexSettings" : [], "allowEdgeOverflow" : false});
        }
    });
